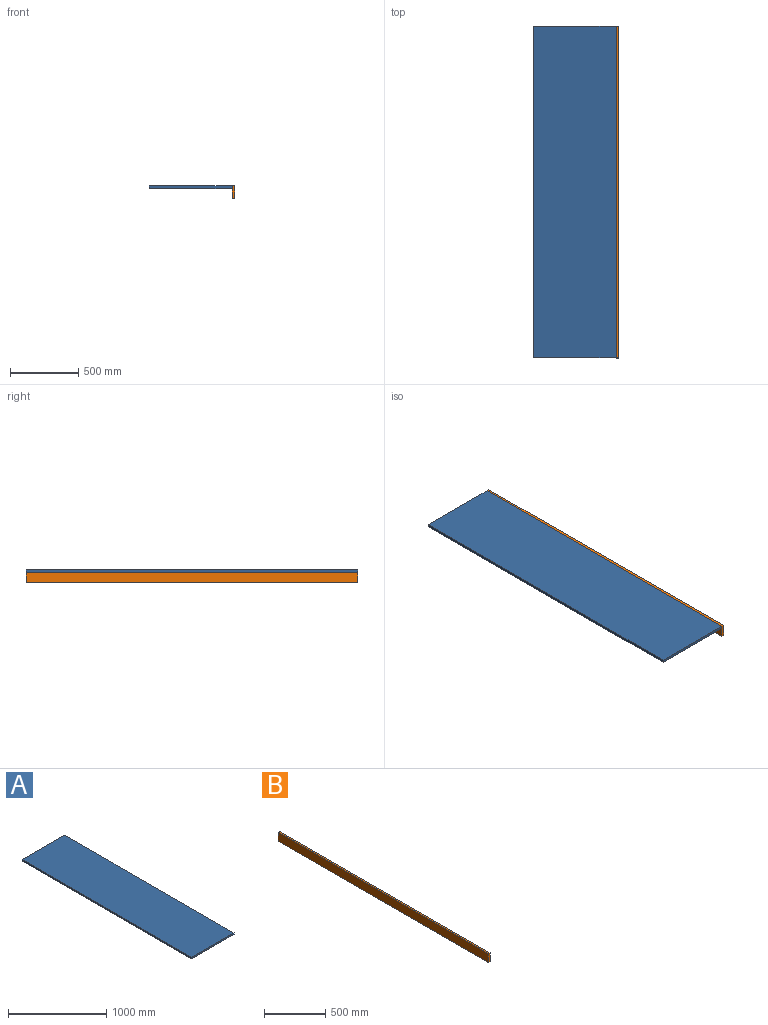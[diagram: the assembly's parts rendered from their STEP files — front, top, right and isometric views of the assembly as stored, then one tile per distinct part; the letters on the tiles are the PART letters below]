
ASSEMBLY  parts=2 mates=1
PART A: 6 faces, bbox 609.6x2438.4x19.1 mm
  f0: plane 2438.4x19.05mm, normal (-1,0,0), area 46451.5mm2, adj f1,f3,f4,f5
  f1: plane 609.6x19.05mm, normal (0,-1,0), area 11612.9mm2, adj f0,f2,f4,f5
  f2: plane 2438.4x19.05mm, normal (1,0,0), area 46451.5mm2, adj f1,f3,f4,f5
  f3: plane 609.6x19.05mm, normal (0,1,0), area 11612.9mm2, adj f0,f2,f4,f5
  f4: plane 2438.4x609.6mm, normal (0,0,1), area 1486448.6mm2, adj f0,f1,f2,f3
  f5: plane 2438.4x609.6mm, normal (0,0,-1), area 1486448.6mm2, adj f0,f1,f2,f3
PART B: 6 faces, bbox 19.1x2438.4x88.9 mm
  f0: plane 2438.4x19.05mm, normal (0,0,1), area 46451.5mm2, adj f1,f3,f4,f5
  f1: plane 88.9x19.05mm, normal (0,-1,0), area 1693.5mm2, adj f0,f2,f3,f4
  f2: plane 2438.4x19.05mm, normal (0,0,-1), area 46451.5mm2, adj f1,f3,f4,f5
  f3: plane 2438.4x88.9mm, normal (1,0,0), area 216773.8mm2, adj f0,f1,f2,f5
  f4: plane 2438.4x88.9mm, normal (-1,0,0), area 216773.8mm2, adj f0,f1,f2,f5
  f5: plane 88.9x19.05mm, normal (0,1,0), area 1693.5mm2, adj f0,f2,f3,f4
PLACE A t=(-333.12,39.51,148.56)mm
PLACE B t=(-8.37,-227.34,4.09)mm
MATE revolute B.f1 <-> A.f1  axis (0,-1,0) through (276.48,39.51,167.61)mm
